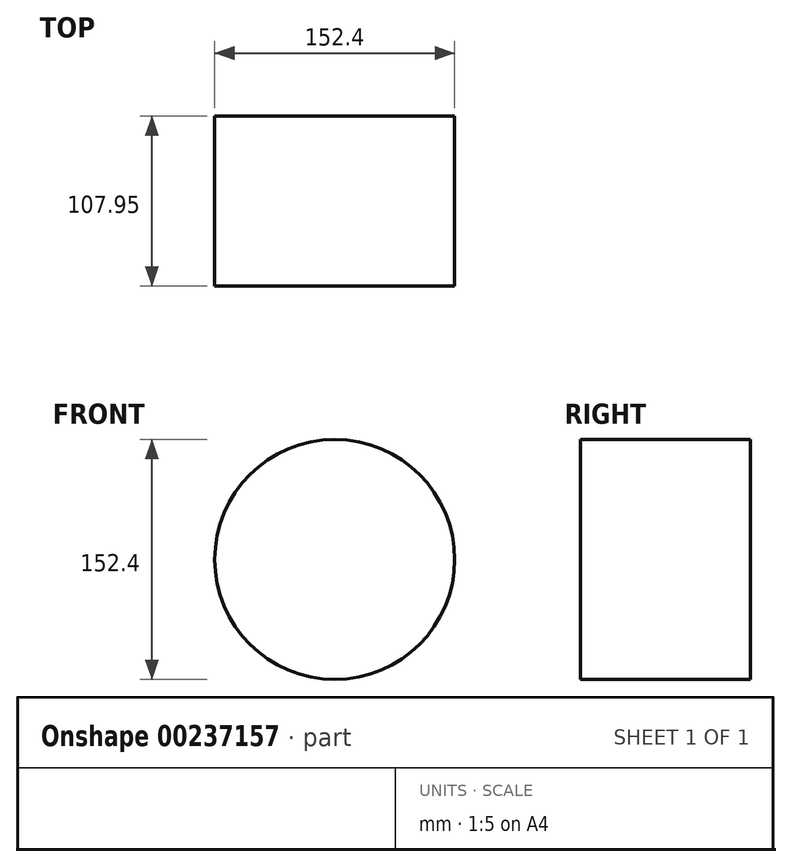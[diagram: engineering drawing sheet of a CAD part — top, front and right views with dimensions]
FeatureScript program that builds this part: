
annotation { "Feature Type Name" : "Feature", "Feature Type Description" : "" }
export const myFeature = defineFeature(function(context is Context, id is Id, definition is map)
    precondition{}
    {
        {
            var Q0;
            Q0=qCreatedBy(makeId("Front.planeOp"),FACE);
            var sketch = newSketch(context, id + "F0", { "sketchPlane" : qUnion([Q0])});
            skCircle(sketch, "E0", {"center": v(0, 0) * mm, "radius": 76.2 * mm});
            skSolve(sketch);
        }
        {
            var Q0;
            Q0 = qSketchRegion(id + "F0", true);
            extrude(context, id + "F1", {"entities" : qUnion([Q0]), "depth" : 107.95 * mm});
        }
    });
